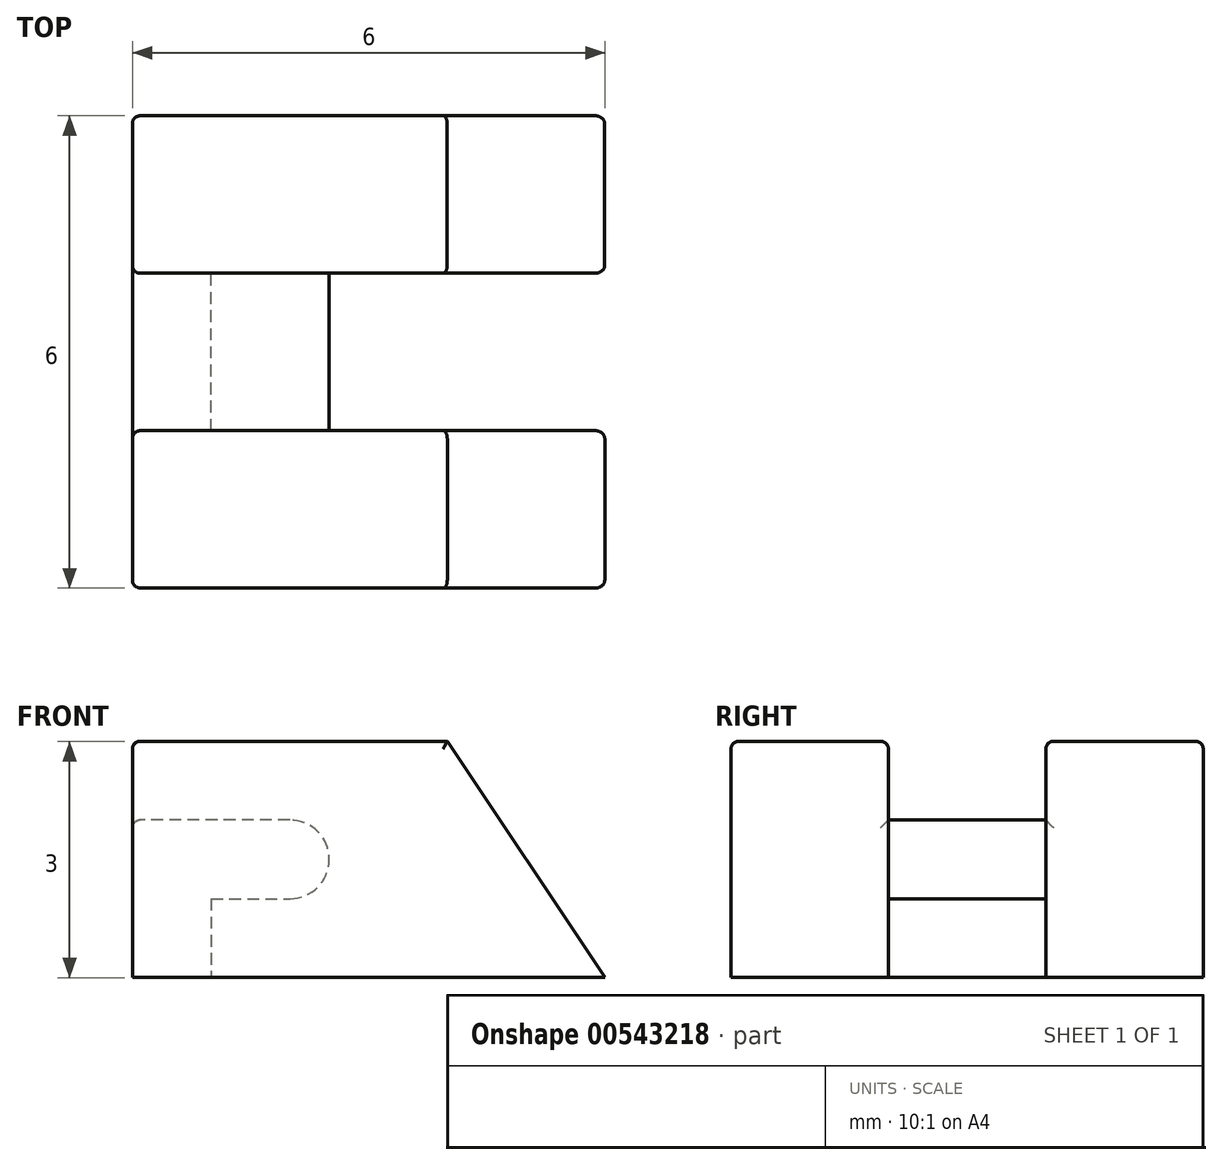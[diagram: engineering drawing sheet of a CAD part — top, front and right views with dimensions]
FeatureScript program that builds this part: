
annotation { "Feature Type Name" : "Feature", "Feature Type Description" : "" }
export const myFeature = defineFeature(function(context is Context, id is Id, definition is map)
    precondition{}
    {
        {
            var Q0;
            Q0=qCreatedBy(makeId("Front.planeOp"),FACE);
            var sketch = newSketch(context, id + "F0", { "sketchPlane" : qUnion([Q0])});
            skLineSegment(sketch, "E0.bottom", {"start": v(-2.2, 0.42) * mm, "end": v(-3.2, 0.42) * mm});
            skLineSegment(sketch, "E0.top", {"start": v(-2.2, -1.58) * mm, "end": v(-3.2, -1.58) * mm});
            skLineSegment(sketch, "E0.left", {"start": v(-2.2, 0.42) * mm, "end": v(-2.2, -1.58) * mm});
            skLineSegment(sketch, "E0.right", {"start": v(-3.2, 0.42) * mm, "end": v(-3.2, -1.58) * mm});
            skPoint(sketch, "E1.center.orphan", {"position": v(-0.53, 0) * mm});
            skLineSegment(sketch, "E2", {"start": v(-2.2, 0.42) * mm, "end": v(-1.2, 0.42) * mm});
            skLineSegment(sketch, "E3", {"start": v(-2.2, -0.58) * mm, "end": v(-1.2, -0.58) * mm});
            skArc(sketch, "E4", {"start": v(-1.2, 0.42) * mm, "mid": v(-0.7, -0.08) * mm, "end": v(-1.2, -0.58) * mm});
            skSolve(sketch);
        }
        {
            var Q0;
            Q0 = qSketchRegion(id + "F0", true);
            extrude(context, id + "F1", {"entities" : qUnion([Q0]), "depth" : 2 * mm, "offsetDistance" : 25 * mm});
        }
        {
            var Q0;
            Q0 = qSketchRegion(id + "F0", true);
            extrude(context, id + "F2", {"entities" : qUnion([Q0]), "operationType" : NewBodyOperationType.ADD, "depth" : 2 * mm, "offsetDistance" : 25 * mm});
        }
        {
            var Q0;
            Q0=qCreatedBy(makeId("Front.planeOp"),FACE);
            var sketch = newSketch(context, id + "F3", { "sketchPlane" : qUnion([Q0])});
            skLineSegment(sketch, "E5.bottom", {"start": v(-3.2, -1.58) * mm, "end": v(0.8, -1.58) * mm});
            skLineSegment(sketch, "E5.top", {"start": v(-3.2, 1.42) * mm, "end": v(0.8, 1.42) * mm});
            skLineSegment(sketch, "E5.left", {"start": v(-3.2, -1.58) * mm, "end": v(-3.2, 1.42) * mm});
            skLineSegment(sketch, "E6", {"start": v(0.8, -1.58) * mm, "end": v(2.8, -1.58) * mm});
            skLineSegment(sketch, "E7", {"start": v(0.8, 1.42) * mm, "end": v(2.8, -1.58) * mm});
            skSolve(sketch);
        }
        {
            var Q0;
            Q0 = qSketchRegion(id + "F3", true);
            extrude(context, id + "F4", {"entities" : qUnion([Q0]), "operationType" : NewBodyOperationType.ADD, "oppositeDirection" : true, "depth" : 2 * mm, "offsetDistance" : 25 * mm});
        }
        {
            var Q0;
            Q0=makeQuery(id+"F4.opExtrude","CAP_FACE",FACE,{"disambiguationData":[OSD([sQuery(id+"F3.wireOp",EDGE,"E5.bottom"),sQuery(id+"F3.wireOp",EDGE,"E5.top"),sQuery(id+"F3.wireOp",EDGE,"E5.left"),sQuery(id+"F3.wireOp",EDGE,"E6"),sQuery(id+"F3.wireOp",EDGE,"E7")])],"isStart":true});
            cPlane(context, id + "F5", {"entities" : qUnion([Q0]), "cplaneType" : CPlaneType.OFFSET, "offset" : 2 * mm, "width" : 150 * mm, "height" : 150 * mm});
        }
        {
            var Q0;
            Q0=qCreatedBy(id+"F5.planeOp",FACE);
            var sketch = newSketch(context, id + "F6", { "sketchPlane" : qUnion([Q0])});
            skLineSegment(sketch, "E8.bottom", {"start": v(-3.2, -1.58) * mm, "end": v(0.8, -1.58) * mm});
            skLineSegment(sketch, "E8.top", {"start": v(-3.2, 1.42) * mm, "end": v(0.8, 1.42) * mm});
            skLineSegment(sketch, "E8.left", {"start": v(-3.2, -1.58) * mm, "end": v(-3.2, 1.42) * mm});
            skLineSegment(sketch, "E9", {"start": v(0.8, -1.58) * mm, "end": v(2.8, -1.58) * mm});
            skLineSegment(sketch, "E10", {"start": v(0.8, 1.42) * mm, "end": v(2.8, -1.58) * mm});
            skSolve(sketch);
        }
        {
            var Q0;
            Q0 = qSketchRegion(id + "F6", true);
            extrude(context, id + "F7", {"entities" : qUnion([Q0]), "operationType" : NewBodyOperationType.ADD, "depth" : 2 * mm, "offsetDistance" : 25 * mm});
        }
        {
            var Q0;
            Q0=makeQuery(id+"F7.opExtrude","CAP_EDGE",EDGE,{"disambiguationData":[OSD([sQuery(id+"F6.wireOp",EDGE,"E10")])],"isStart":false});
            var Q1;
            Q1=makeQuery(id+"F4.opExtrude","CAP_EDGE",EDGE,{"disambiguationData":[OSD([sQuery(id+"F3.wireOp",EDGE,"E7")])],"isStart":false});
            var Q2;
            Q2=makeQuery(id+"F4.opExtrude","CAP_EDGE",EDGE,{"disambiguationData":[OSD([sQuery(id+"F3.wireOp",EDGE,"E7")])],"isStart":true});
            var Q3;
            Q3=makeQuery(id+"F7.opExtrude","CAP_EDGE",EDGE,{"disambiguationData":[OSD([sQuery(id+"F6.wireOp",EDGE,"E10")])],"isStart":true});
            var Q4;
            Q4=makeQuery(id+"F7.opExtrude","CAP_EDGE",EDGE,{"disambiguationData":[OSD([sQuery(id+"F6.wireOp",EDGE,"E8.top")])],"isStart":false});
            var Q5;
            Q5=makeQuery(id+"F7.opExtrude","CAP_EDGE",EDGE,{"disambiguationData":[OSD([sQuery(id+"F6.wireOp",EDGE,"E8.top")])],"isStart":true});
            var Q6;
            Q6=makeQuery(id+"F4.opExtrude","CAP_EDGE",EDGE,{"disambiguationData":[OSD([sQuery(id+"F3.wireOp",EDGE,"E5.top")])],"isStart":true});
            var Q7;
            Q7=makeQuery(id+"F4.opExtrude","CAP_EDGE",EDGE,{"disambiguationData":[OSD([sQuery(id+"F3.wireOp",EDGE,"E5.top")])],"isStart":false});
            var Q8;
            Q8=makeQuery(id+"F7.opExtrude","SWEPT_EDGE",EDGE,{"disambiguationData":[OSD([sQuery(id+"F6.wireOp",EDGE,"E8.top"),sQuery(id+"F6.wireOp",EDGE,"E8.left")])]});
            var Q9;
            Q9=makeQuery(id+"F4.opExtrude","SWEPT_EDGE",EDGE,{"disambiguationData":[OSD([sQuery(id+"F3.wireOp",EDGE,"E5.top"),sQuery(id+"F3.wireOp",EDGE,"E5.left")])]});
            var Q10;
            Q10=makeQuery(id+"F7.opExtrude","CAP_EDGE",EDGE,{"disambiguationData":[OSD([sQuery(id+"F6.wireOp",EDGE,"E8.left")])],"isStart":false});
            var Q11;
            Q11=makeQuery(id+"F4.opExtrude","CAP_EDGE",EDGE,{"disambiguationData":[OSD([sQuery(id+"F3.wireOp",EDGE,"E5.left")])],"isStart":false});
            var Q12;
            Q12=makeQuery(id+"F4.boolean.opBoolean","SPLIT",EDGE,{"derivedFrom":makeQuery(id+"F4.opExtrude","CAP_EDGE",EDGE,{"disambiguationData":[OSD([sQuery(id+"F3.wireOp",EDGE,"E5.left")])],"isStart":true})});
            var Q13;
            Q13=makeQuery(id+"F7.boolean.opBoolean","SPLIT",EDGE,{"derivedFrom":makeQuery(id+"F7.opExtrude","CAP_EDGE",EDGE,{"disambiguationData":[OSD([sQuery(id+"F6.wireOp",EDGE,"E8.left")])],"isStart":true})});
            var Q14;
            Q14=makeQuery(id+"F1.opExtrude","SWEPT_EDGE",EDGE,{"disambiguationData":[OSD([sQuery(id+"F0.wireOp",EDGE,"E0.bottom"),sQuery(id+"F0.wireOp",EDGE,"E0.right")])]});
            fillet(context, id + "F8", {"entities" : qUnion([Q0, Q1, Q2, Q3, Q4, Q5, Q6, Q7, Q8, Q9, Q10, Q11, Q12, Q13, Q14]), "radius" : 0.1 * mm, "tangentPropagation" : true, "allowEdgeOverflow" : false});
        }
    });
